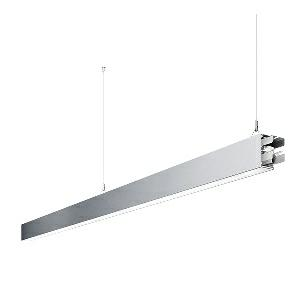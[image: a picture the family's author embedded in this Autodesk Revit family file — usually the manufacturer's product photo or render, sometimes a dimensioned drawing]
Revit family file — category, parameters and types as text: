
# Revit family: idoo_line_-_ilp_6000_840_d_mid_00805706_89ac
name_source: partatom
category: Lighting Fixtures
units: mm (PartAtom-declared; Revit-internal decimal feet)

## family parameters
Cut with Voids When Loaded = No
Host = Face
Light Source = No
Part Type = Normal
Room Calculation Point = No
Round Connector Dimension = Use Diameter
Shared = No

## types (1)
- IDOO.line - ILP 6000/840/D MID (1 x LED, 6300 lm, 4000K)
    Apparent Load = 46 VA
    Approval mark = CE
    CIE Flux Codes = 66 91 98 40 100
    Color Rendering = 80-89
    Color Temperature = 4000K
    Control Gear = Electronic ballast
    Default Elevation = 1800 mm
    Description = ILP 6000/840/D|Suspended luminaire|light source: LED|connected load: 220-240 V, 50/60 Hz|Power consumption: approx. 46 W|standby: approx. 0,15|luminous flux: 6300 lm|luminous efficacy: 136 lm/W|light distribution: Direct/indirect|direct ratio: approx. 40 %|colour temperature: Cold white, ca. 4000 K|color rendering index (CRI): >= 80|chromaticity tolerance:  3 SDCM|System of protection: IP 40|technology: Continuously dimmable|luminaire body|material: Sectional aluminium|colour: Silver|lamp cover: Acrylic (PMMA), Clear|mains lead: 1,0 m With free stranded wires|Fastening: Steel cable 0.3 - 0.7 m|glare control: Prism aperture|luminance(L65): <= 2700 cd/m|unified glare rating(4H 8H): <=  16|special features: DALI Load 1x, TouchDIM - dimming via standard switch, Through-wired, up to 18 m on one mains connection, Flicker-free, Suitable as emergency lighting, Mechanical and electrical connection of the individual modules without tools|
    Frequency = 50 Hz
    Height = 110 mm
    Lamp = 1 x LED
    Lamp Light Flux = 6300 lm
    Lamp count = 1
    Length = 2244 mm
    Luminous efficacy = 137 lm/W
    Manufacturer = Waldmann
    ModVariant = No
    Model = 00805706
    Mounting Place = Ceiling
    Mounting Type = Pendant
    Number of Poles = 1
    OnlyDefault = Yes
    Power Factor = 1
    Product Name = IDOO.line - ILP 6000/840/D MID
    Product group = Suspended luminaire
    ProductGroupID = 9
    Protection Class = Protection class I
    Protection Degree = IP 40
    RLX_Detail_Level = 1
    RLX_Emergency_Light_Flux = 0 lm
    RLX_Emergency_Type = 0
    RLX_Emergency_Type_DB = No
    RlxData = <blob elided: 24029 chars, md5=edc377ea>
    Socket = socket
    Standby Power = 0 W
    System Light Flux = 6300 lm
    System Power = 46 W
    Type Comments = Product without accessories
    Type Image = 113317000-00692618.jpg
    URL = http://relux.com
    VarID = ---
    Voltage = 230 V
    Voltage Range = 220-240 V
    Weight = 0.00 kg
    Width = 60 mm  [stored 0.19685 ft]

note: [stored X ft] marks values corroborated as IEEE doubles in the binary element streams (Revit-internal decimal feet)

## geometry (parser evidence)
native form markers: Blend x4, Sweep x15
no freeform markers — native parametric forms only
